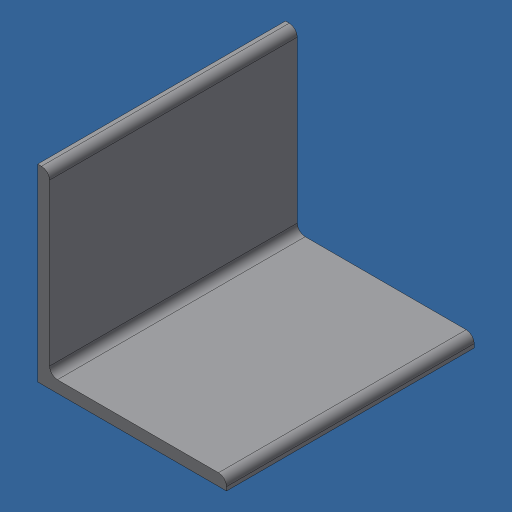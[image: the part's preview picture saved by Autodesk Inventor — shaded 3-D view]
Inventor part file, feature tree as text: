
AUTODESK INVENTOR PART (.ipt)
format: ipt  version: 2024.3 (Build 283343000, 343)  size: 118,272 bytes
history: native  units: mm (DEFAULTED — no unit token found)
features: other x1, extrude x1
ambient origin geometry x8: Origin, YZ Plane, XZ Plane, XY Plane, X Axis, Y Axis, Z Axis, Center Point
bodies: Body1 (feature_tree)
feature tree (2):
  other  "Finish - None"
  extrude  "3" X 3" X 3/16""  Depth=4.7625mm
